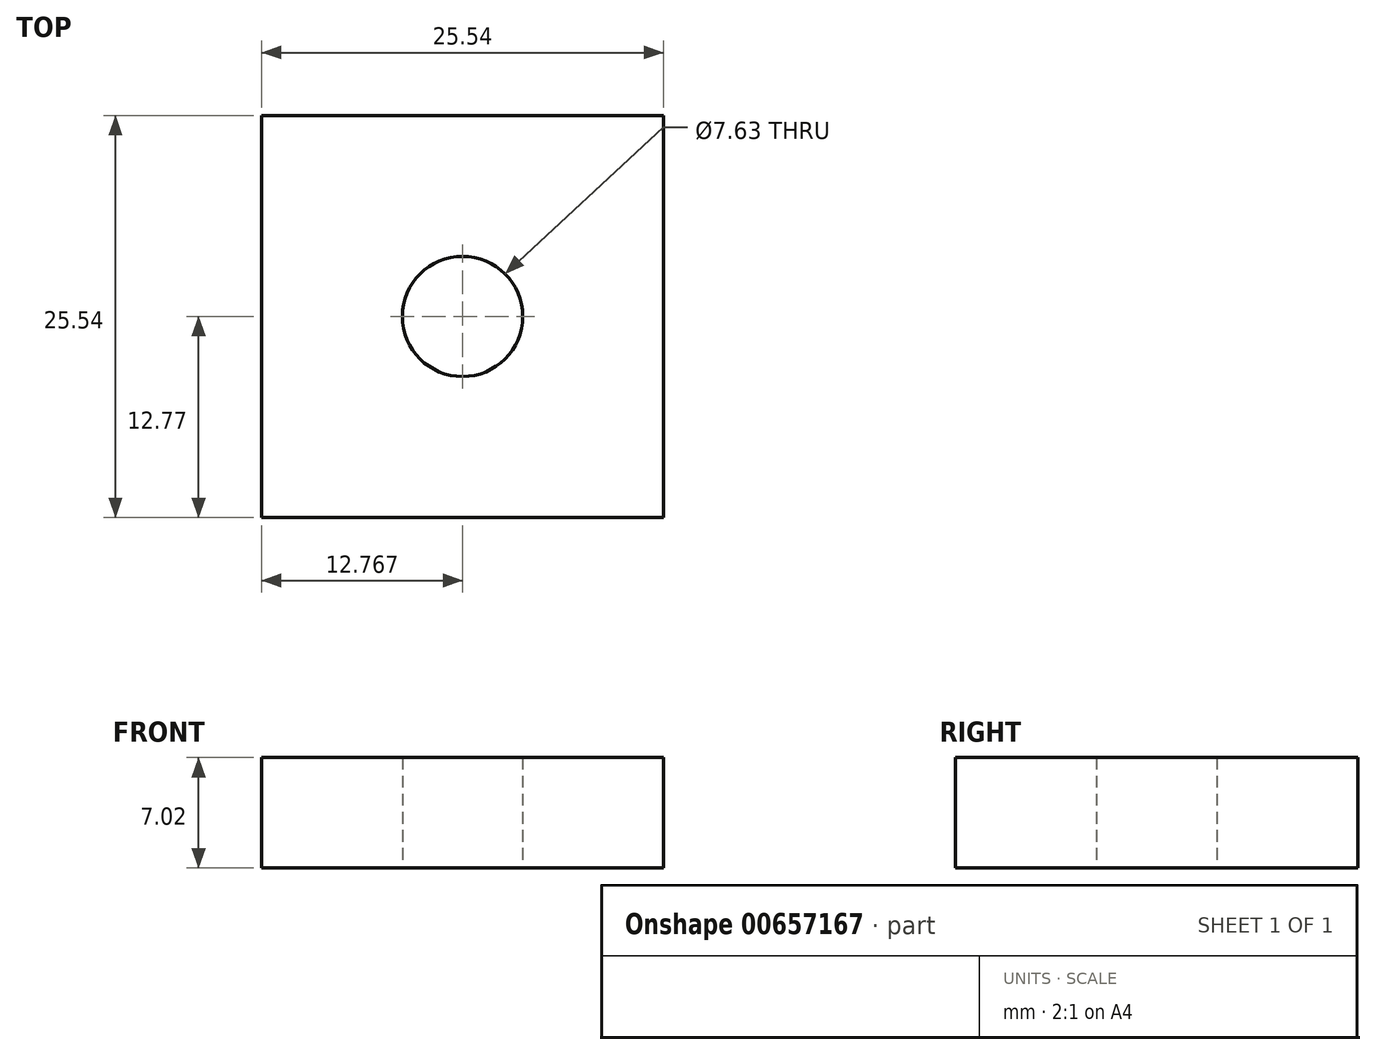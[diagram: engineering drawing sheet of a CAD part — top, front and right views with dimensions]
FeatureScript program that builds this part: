
annotation { "Feature Type Name" : "Feature", "Feature Type Description" : "" }
export const myFeature = defineFeature(function(context is Context, id is Id, definition is map)
    precondition{}
    {
        {
            var Q0;
            Q0=qCreatedBy(makeId("Top.planeOp"),FACE);
            var sketch = newSketch(context, id + "F0", { "sketchPlane" : qUnion([Q0])});
            skLineSegment(sketch, "E0.bottom", {"start": v(-10.17, 12.77) * mm, "end": v(-35.71, 12.77) * mm});
            skLineSegment(sketch, "E0.top", {"start": v(-10.17, -12.77) * mm, "end": v(-35.71, -12.77) * mm});
            skLineSegment(sketch, "E0.left", {"start": v(-35.71, -12.77) * mm, "end": v(-35.71, 12.77) * mm});
            skLineSegment(sketch, "E0.right", {"start": v(-10.17, -12.77) * mm, "end": v(-10.17, 12.77) * mm});
            skPoint(sketch, "E0.middle", {"position": v(-22.94, 0) * mm});
            skCircle(sketch, "E1", {"center": v(-22.94, 0) * mm, "radius": 3.82 * mm});
            skSolve(sketch);
        }
        {
            var Q0;
            Q0=makeQuery(id+"F0.imprint","IMPRINT",FACE,{"disambiguationData":[TD([[makeQuery(id+"F0.imprint","IMPRINT",EDGE,{"derivedFrom":sQuery(id+"F0.wireOp",EDGE,"E0.bottom")}),1.0]])]});
            extrude(context, id + "F1", {"entities" : qUnion([Q0]), "depth" : 7.02 * mm, "offsetDistance" : 25 * mm});
        }
    });
